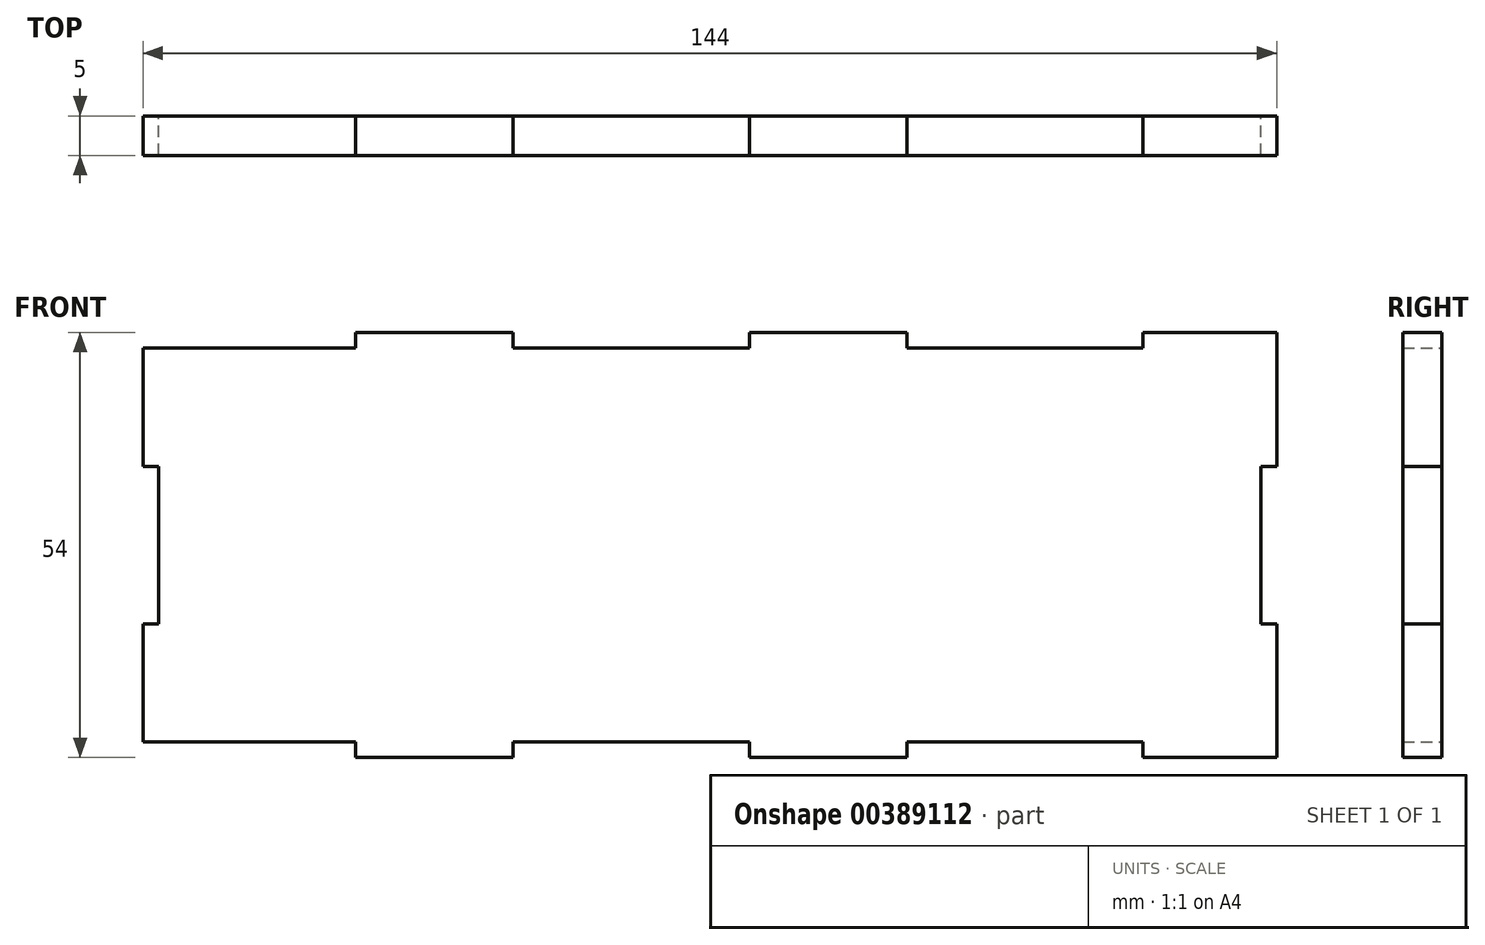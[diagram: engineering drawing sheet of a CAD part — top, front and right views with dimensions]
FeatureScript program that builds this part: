
annotation { "Feature Type Name" : "Feature", "Feature Type Description" : "" }
export const myFeature = defineFeature(function(context is Context, id is Id, definition is map)
    precondition{}
    {
        {
            var Q0;
            Q0=qCreatedBy(makeId("Front.planeOp"),FACE);
            var sketch = newSketch(context, id + "F0", { "sketchPlane" : qUnion([Q0])});
            skLineSegment(sketch, "E0", {"start": v(0, 0) * mm, "end": v(0, 15) * mm});
            skLineSegment(sketch, "E1", {"start": v(0, 15) * mm, "end": v(2, 15) * mm});
            skLineSegment(sketch, "E2", {"start": v(2, 15) * mm, "end": v(2, 35) * mm});
            skLineSegment(sketch, "E3", {"start": v(2, 35) * mm, "end": v(0, 35) * mm});
            skLineSegment(sketch, "E4", {"start": v(0, 35) * mm, "end": v(0, 50) * mm});
            skLineSegment(sketch, "E5", {"start": v(0, 50) * mm, "end": v(27, 50) * mm});
            skLineSegment(sketch, "E6", {"start": v(27, 50) * mm, "end": v(27, 52) * mm});
            skLineSegment(sketch, "E7", {"start": v(27, 52) * mm, "end": v(47, 52) * mm});
            skLineSegment(sketch, "E8", {"start": v(47, 52) * mm, "end": v(47, 50) * mm});
            skLineSegment(sketch, "E9", {"start": v(47, 50) * mm, "end": v(77, 50) * mm});
            skLineSegment(sketch, "E10", {"start": v(77, 50) * mm, "end": v(77, 52) * mm});
            skLineSegment(sketch, "E11", {"start": v(77, 52) * mm, "end": v(97, 52) * mm});
            skLineSegment(sketch, "E12", {"start": v(97, 52) * mm, "end": v(97, 50) * mm});
            skLineSegment(sketch, "E13", {"start": v(97, 50) * mm, "end": v(127, 50) * mm});
            skLineSegment(sketch, "E14", {"start": v(127, 50) * mm, "end": v(127, 52) * mm});
            skLineSegment(sketch, "E15", {"start": v(127, 52) * mm, "end": v(144, 52) * mm});
            skLineSegment(sketch, "E16", {"start": v(144, 52) * mm, "end": v(144, 35) * mm});
            skLineSegment(sketch, "E17", {"start": v(144, 35) * mm, "end": v(142, 35) * mm});
            skLineSegment(sketch, "E18", {"start": v(142, 35) * mm, "end": v(142, 15) * mm});
            skLineSegment(sketch, "E19", {"start": v(142, 15) * mm, "end": v(144, 15) * mm});
            skLineSegment(sketch, "E20", {"start": v(144, 15) * mm, "end": v(144, -2) * mm});
            skLineSegment(sketch, "E21", {"start": v(144, -2) * mm, "end": v(127, -2) * mm});
            skLineSegment(sketch, "E22", {"start": v(127, -2) * mm, "end": v(127, 0) * mm});
            skLineSegment(sketch, "E23", {"start": v(127, 0) * mm, "end": v(97, 0) * mm});
            skLineSegment(sketch, "E24", {"start": v(97, 0) * mm, "end": v(97, -2) * mm});
            skLineSegment(sketch, "E25", {"start": v(97, -2) * mm, "end": v(77, -2) * mm});
            skPoint(sketch, "E25.endSnap0", {"position": v(77, 51) * mm});
            skLineSegment(sketch, "E26", {"start": v(77, -2) * mm, "end": v(77, 0) * mm});
            skLineSegment(sketch, "E27", {"start": v(77, 0) * mm, "end": v(47, 0) * mm});
            skLineSegment(sketch, "E28", {"start": v(47, 0) * mm, "end": v(47, -2) * mm});
            skLineSegment(sketch, "E29", {"start": v(47, -2) * mm, "end": v(27, -2) * mm});
            skLineSegment(sketch, "E30", {"start": v(27, -2) * mm, "end": v(27, 0) * mm});
            skLineSegment(sketch, "E31", {"start": v(27, 0) * mm, "end": v(0, 0) * mm});
            skSolve(sketch);
        }
        {
            var Q0;
            Q0=makeQuery(id+"F0.imprint","IMPRINT",FACE,{"disambiguationData":[TD([[makeQuery(id+"F0.imprint","IMPRINT",EDGE,{"derivedFrom":sQuery(id+"F0.wireOp",EDGE,"E0")}),-1.0]])]});
            extrude(context, id + "F1", {"entities" : qUnion([Q0]), "depth" : 5 * mm});
        }
    });
